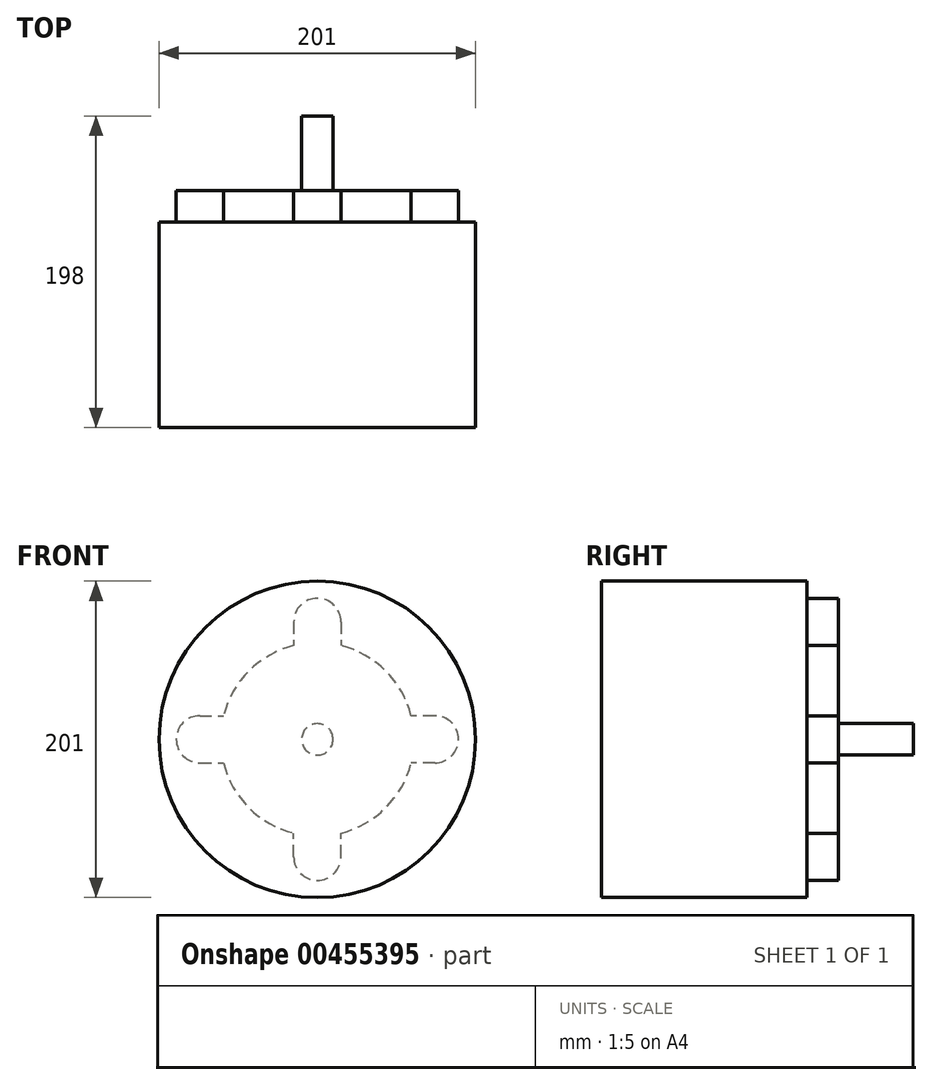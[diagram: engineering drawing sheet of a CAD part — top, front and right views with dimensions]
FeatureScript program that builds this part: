
annotation { "Feature Type Name" : "Feature", "Feature Type Description" : "" }
export const myFeature = defineFeature(function(context is Context, id is Id, definition is map)
    precondition{}
    {
        {
            var Q0;
            Q0=qCreatedBy(makeId("Right.planeOp"),FACE);
            var sketch = newSketch(context, id + "F0", { "sketchPlane" : qUnion([Q0])});
            skLineSegment(sketch, "E0", {"start": v(-75.25, 0) * mm, "end": v(122.75, 0) * mm});
            skLineSegment(sketch, "E1", {"start": v(122.75, 0) * mm, "end": v(122.75, 10) * mm});
            skLineSegment(sketch, "E2", {"start": v(122.75, 10) * mm, "end": v(75.25, 10) * mm});
            skLineSegment(sketch, "E3", {"start": v(75.25, 10) * mm, "end": v(75.25, 100.5) * mm});
            skLineSegment(sketch, "E4", {"start": v(75.25, 100.5) * mm, "end": v(-75.25, 100.5) * mm});
            skLineSegment(sketch, "E5", {"start": v(-75.25, 100.5) * mm, "end": v(-75.25, 0) * mm});
            skSolve(sketch);
        }
        {
            var Q0;
            Q0=makeQuery(id+"F0.imprint","IMPRINT",FACE,{"disambiguationData":[TD([[makeQuery(id+"F0.imprint","IMPRINT",EDGE,{"derivedFrom":sQuery(id+"F0.wireOp",EDGE,"E0")}),1.0]])]});
            var Q1;
            Q1=sQuery(id+"F0.wireOp",EDGE,"E0");
            revolve(context, id + "F1", {"entities" : qUnion([Q0]), "axis" : qUnion([Q1]), "revolveType" : RevolveType.FULL});
        }
        {
            var Q0;
            Q0=makeQuery(id+"F1.opRevolve","SWEPT_FACE",FACE,{"disambiguationData":[OSD([sQuery(id+"F0.wireOp",EDGE,"E3")])]});
            var sketch = newSketch(context, id + "F2", { "sketchPlane" : qUnion([Q0])});
            skCircle(sketch, "E6", {"center": v(0, 0) * mm, "radius": 115 * mm});
            skCircle(sketch, "E7", {"center": v(0, 0) * mm, "radius": 74.6 * mm, "construction": true});
            skCircle(sketch, "E8", {"center": v(0, 74.6) * mm, "radius": 5 * mm});
            skCircle(sketch, "E9.1.0", {"center": v(-74.6, 0) * mm, "radius": 5 * mm});
            skCircle(sketch, "E9.2.0", {"center": v(0, -74.6) * mm, "radius": 5 * mm});
            skCircle(sketch, "E9.3.0", {"center": v(74.6, 0) * mm, "radius": 5 * mm});
            skArc(sketch, "E10", {"start": v(15, 74.6) * mm, "mid": v(0, 89.6) * mm, "end": v(-15, 74.6) * mm});
            skLineSegment(sketch, "E11", {"start": v(15, 74.6) * mm, "end": v(15, 59.6) * mm});
            skLineSegment(sketch, "E12", {"start": v(-15, 74.6) * mm, "end": v(-15, 59.6) * mm});
            skArc(sketch, "E13", {"start": v(15, 59.6) * mm, "mid": v(43.46, 43.46) * mm, "end": v(59.6, 15) * mm});
            skArc(sketch, "E14", {"start": v(-15, 59.6) * mm, "mid": v(-43.46, 43.46) * mm, "end": v(-59.6, 15) * mm});
            skArc(sketch, "E15", {"start": v(74.6, -15) * mm, "mid": v(89.6, 0) * mm, "end": v(74.6, 15) * mm});
            skArc(sketch, "E16", {"start": v(-74.6, -15) * mm, "mid": v(-89.6, 0) * mm, "end": v(-74.6, 15) * mm});
            skLineSegment(sketch, "E17", {"start": v(74.6, 15) * mm, "end": v(59.6, 15) * mm});
            skLineSegment(sketch, "E18", {"start": v(74.6, -15) * mm, "end": v(59.6, -15) * mm});
            skLineSegment(sketch, "E19", {"start": v(-74.6, 15) * mm, "end": v(-59.6, 15) * mm});
            skLineSegment(sketch, "E20", {"start": v(-74.6, -15) * mm, "end": v(-59.6, -15) * mm});
            skArc(sketch, "E21", {"start": v(59.6, -15) * mm, "mid": v(43.46, -43.46) * mm, "end": v(15, -59.6) * mm});
            skArc(sketch, "E22", {"start": v(-59.6, -15) * mm, "mid": v(-43.46, -43.46) * mm, "end": v(-15, -59.6) * mm});
            skArc(sketch, "E23", {"start": v(15, -74.6) * mm, "mid": v(0, -89.6) * mm, "end": v(-15, -74.6) * mm});
            skLineSegment(sketch, "E24", {"start": v(15, -74.6) * mm, "end": v(15, -59.6) * mm});
            skLineSegment(sketch, "E25", {"start": v(-15, -74.6) * mm, "end": v(-15, -59.6) * mm});
            skSolve(sketch);
        }
        {
            var Q0;
            Q0 = qSketchRegion(id + "F2", true);
            extrude(context, id + "F3", {"entities" : qUnion([Q0]), "operationType" : NewBodyOperationType.REMOVE, "oppositeDirection" : true, "depth" : 20 * mm});
        }
    });
